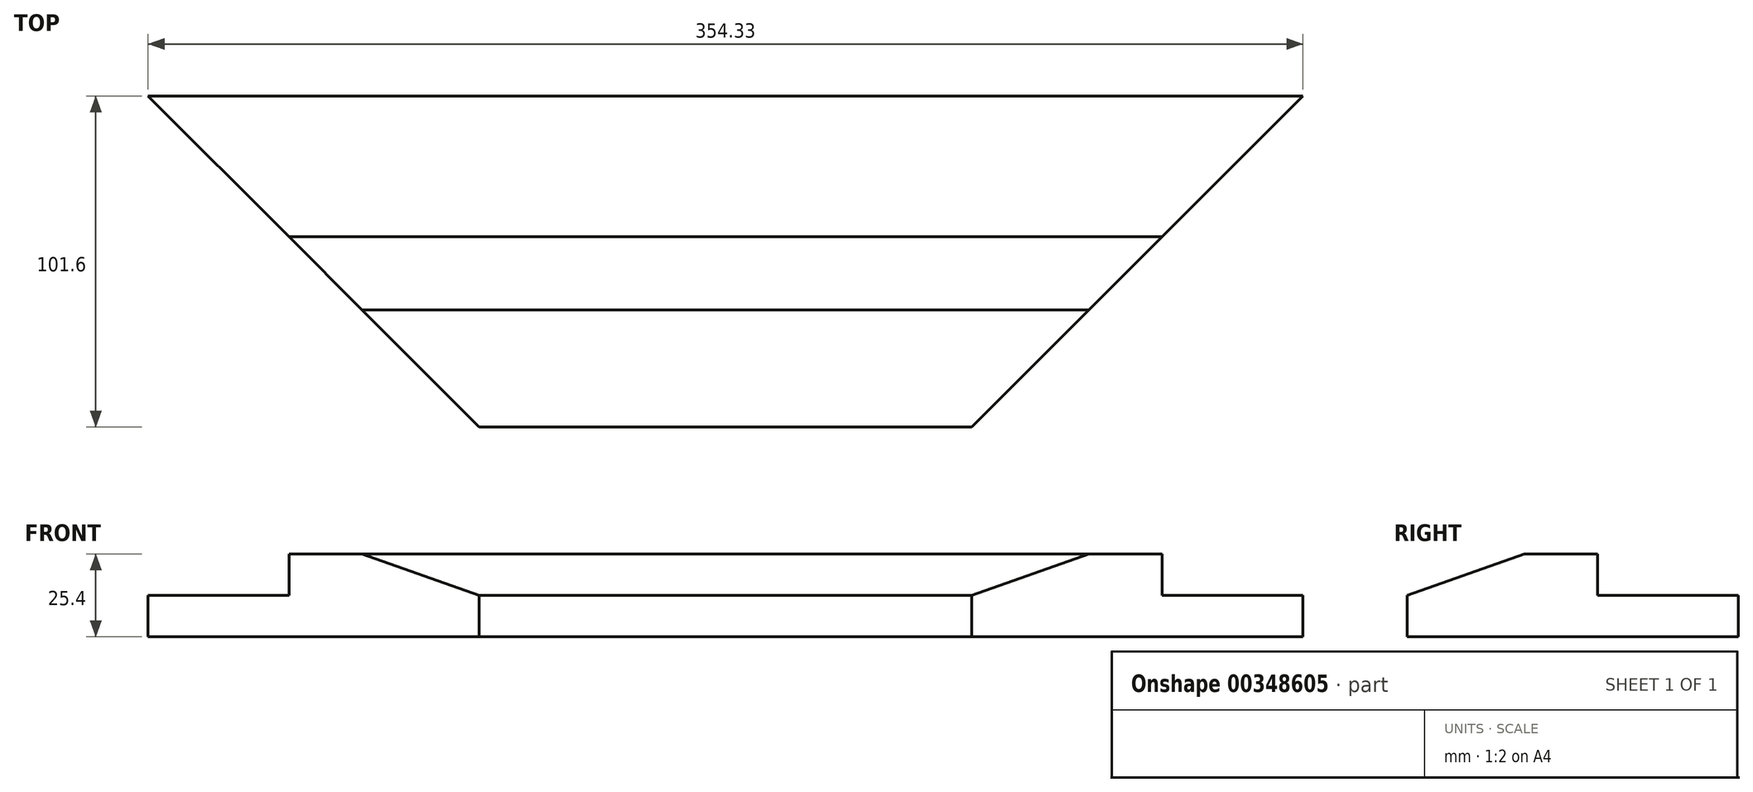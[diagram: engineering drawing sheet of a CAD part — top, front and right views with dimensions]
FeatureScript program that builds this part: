
annotation { "Feature Type Name" : "Feature", "Feature Type Description" : "" }
export const myFeature = defineFeature(function(context is Context, id is Id, definition is map)
    precondition{}
    {
        {
            var Q0;
            Q0=qCreatedBy(makeId("Top.planeOp"),FACE);
            var sketch = newSketch(context, id + "F0", { "sketchPlane" : qUnion([Q0])});
            skLineSegment(sketch, "E0", {"start": v(-196.23, 9.2) * mm, "end": v(-45.1, 9.2) * mm});
            skLineSegment(sketch, "E1", {"start": v(-45.1, 9.2) * mm, "end": v(56.5, 110.8) * mm});
            skLineSegment(sketch, "E2", {"start": v(56.5, 110.8) * mm, "end": v(-297.83, 110.8) * mm});
            skLineSegment(sketch, "E3", {"start": v(-297.83, 110.8) * mm, "end": v(-196.23, 9.2) * mm});
            skLineSegment(sketch, "E4", {"start": v(-254.6, 67.57) * mm, "end": v(13.27, 67.57) * mm});
            skSolve(sketch);
        }
        {
            var Q0;
            {var subQ0=sQuery(id+"F0.wireOp",EDGE,"E0");Q0=makeQuery(id+"F0.imprint","IMPRINT",FACE,{"disambiguationData":[TD([[makeQuery(id+"F0.imprint","IMPRINT",EDGE,{"derivedFrom":subQ0}),1.0]])]});}
            extrude(context, id + "F1", {"entities" : qUnion([Q0]), "depth" : 12.7 * mm});
        }
        {
            var Q0;
            Q0 = qSketchRegion(id + "F0", true);
            extrude(context, id + "F2", {"entities" : qUnion([Q0]), "operationType" : NewBodyOperationType.ADD, "depth" : -12.7 * mm});
        }
        {
            var Q0;
            Q0=makeQuery(id+"F1.opExtrude","CAP_EDGE",EDGE,{"disambiguationData":[OSD([sQuery(id+"F0.wireOp",EDGE,"E0")])],"isStart":false});
            chamfer(context, id + "F3", {"entities" : qUnion([Q0]), "chamferType" : ChamferType.TWO_OFFSETS, "width1" : 35.92 * mm, "oppositeDirection" : false, "width2" : 12.7 * mm, "tangentPropagation" : true});
        }
    });
